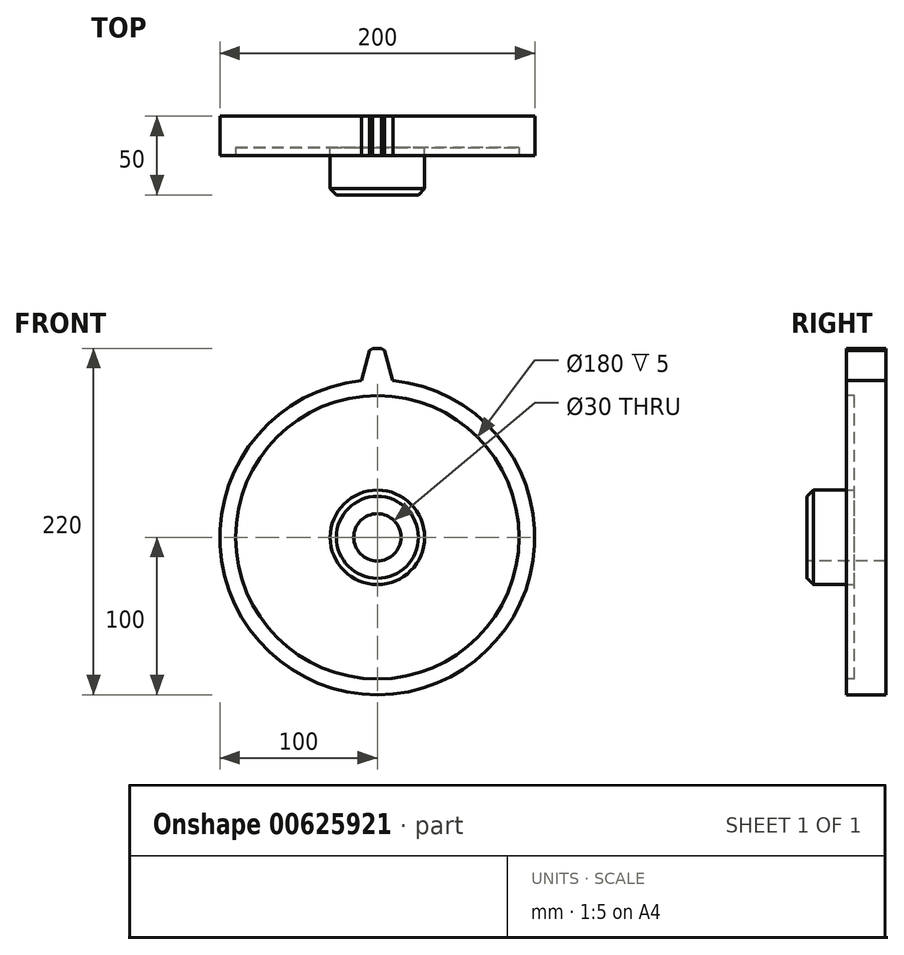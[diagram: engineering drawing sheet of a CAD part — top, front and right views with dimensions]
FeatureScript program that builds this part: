
annotation { "Feature Type Name" : "Feature", "Feature Type Description" : "" }
export const myFeature = defineFeature(function(context is Context, id is Id, definition is map)
    precondition{}
    {
        {
            var Q0;
            Q0=qCreatedBy(makeId("Front.planeOp"),FACE);
            var sketch = newSketch(context, id + "F0", { "sketchPlane" : qUnion([Q0])});
            skCircle(sketch, "E0", {"center": v(0, 0) * mm, "radius": 100 * mm});
            skSolve(sketch);
        }
        {
            var Q0;
            Q0=qCreatedBy(makeId("Front.planeOp"),FACE);
            var sketch = newSketch(context, id + "F1", { "sketchPlane" : qUnion([Q0])});
            skLineSegment(sketch, "E1", {"start": v(9.81, 99.52) * mm, "end": v(-10.17, 99.48) * mm});
            skLineSegment(sketch, "E2", {"start": v(-10.17, 99.48) * mm, "end": v(-4.72, 120) * mm});
            skLineSegment(sketch, "E3", {"start": v(-4.72, 120) * mm, "end": v(4.28, 120) * mm});
            skLineSegment(sketch, "E4", {"start": v(4.28, 120) * mm, "end": v(9.81, 99.52) * mm});
            skSolve(sketch);
        }
        {
            var Q0;
            Q0=qSketchRegion(id+"F0",true);
            extrude(context, id + "F2", {"entities" : qUnion([Q0]), "depth" : 25 * mm, "offsetDistance" : 25 * mm});
        }
        {
            var Q0;
            Q0=makeQuery(id+"F1.imprint","IMPRINT",FACE,{"disambiguationData":[TD([[makeQuery(id+"F1.imprint","IMPRINT",EDGE,{"derivedFrom":sQuery(id+"F1.wireOp",EDGE,"E1")}),-1.0]])]});
            var Q1;
            Q1=makeQuery(id+"F2.opExtrude","CAP_FACE",FACE,{"disambiguationData":[OSD([sQuery(id+"F0.wireOp",EDGE,"E0")])],"isStart":false});
            extrude(context, id + "F3", {"entities" : qUnion([Q0]), "operationType" : NewBodyOperationType.ADD, "endBound" : BoundingType.UP_TO_SURFACE, "depth" : 25 * mm, "endBoundEntityFace" : qUnion([Q1]), "offsetDistance" : 25 * mm});
        }
        {
            var Q0;
            Q0=makeQuery(id+"F3.opExtrude","SWEPT_EDGE",EDGE,{"disambiguationData":[OSD([sQuery(id+"F1.wireOp",EDGE,"E1"),sQuery(id+"F1.wireOp",EDGE,"E2")])]});
            var Q1;
            Q1=makeQuery(id+"F3.opExtrude","SWEPT_EDGE",EDGE,{"disambiguationData":[OSD([sQuery(id+"F1.wireOp",EDGE,"E1"),sQuery(id+"F1.wireOp",EDGE,"E4")])]});
            fillet(context, id + "F4", {"entities" : qUnion([Q0, Q1]), "radius" : 5 * mm, "tangentPropagation" : true, "allowEdgeOverflow" : false});
        }
        {
            var Q0;
            Q0=makeQuery(id+"F3.opExtrude","SWEPT_EDGE",EDGE,{"disambiguationData":[OSD([sQuery(id+"F1.wireOp",EDGE,"E2"),sQuery(id+"F1.wireOp",EDGE,"E3")])]});
            var Q1;
            Q1=makeQuery(id+"F3.opExtrude","SWEPT_EDGE",EDGE,{"disambiguationData":[OSD([sQuery(id+"F1.wireOp",EDGE,"E3"),sQuery(id+"F1.wireOp",EDGE,"E4")])]});
            chamfer(context, id + "F5", {"entities" : qUnion([Q0, Q1]), "width" : 2 * mm, "tangentPropagation" : true});
        }
        {
            var Q0;
            {var subQ0=sQuery(id+"F0.wireOp",EDGE,"E0");Q0=makeQuery(id+"FKvSvNCsyhTZhGM_1.19.F3.boolean.opBoolean","MERGE",FACE,{"derivedFrom":[makeQuery(id+"FKvSvNCsyhTZhGM_1.18.F3.boolean.opBoolean","MERGE",FACE,{"derivedFrom":[makeQuery(id+"FKvSvNCsyhTZhGM_1.17.F3.boolean.opBoolean","MERGE",FACE,{"derivedFrom":[makeQuery(id+"FKvSvNCsyhTZhGM_1.16.F3.boolean.opBoolean","MERGE",FACE,{"derivedFrom":[makeQuery(id+"FKvSvNCsyhTZhGM_1.15.F3.boolean.opBoolean","MERGE",FACE,{"derivedFrom":[makeQuery(id+"FKvSvNCsyhTZhGM_1.14.F3.boolean.opBoolean","MERGE",FACE,{"derivedFrom":[makeQuery(id+"FKvSvNCsyhTZhGM_1.13.F3.boolean.opBoolean","MERGE",FACE,{"derivedFrom":[makeQuery(id+"FKvSvNCsyhTZhGM_1.12.F3.boolean.opBoolean","MERGE",FACE,{"derivedFrom":[makeQuery(id+"FKvSvNCsyhTZhGM_1.11.F3.boolean.opBoolean","MERGE",FACE,{"derivedFrom":[makeQuery(id+"FKvSvNCsyhTZhGM_1.10.F3.boolean.opBoolean","MERGE",FACE,{"derivedFrom":[makeQuery(id+"FKvSvNCsyhTZhGM_1.9.F3.boolean.opBoolean","MERGE",FACE,{"derivedFrom":[makeQuery(id+"FKvSvNCsyhTZhGM_1.8.F3.boolean.opBoolean","MERGE",FACE,{"derivedFrom":[makeQuery(id+"FKvSvNCsyhTZhGM_1.7.F3.boolean.opBoolean","MERGE",FACE,{"derivedFrom":[makeQuery(id+"FKvSvNCsyhTZhGM_1.6.F3.boolean.opBoolean","MERGE",FACE,{"derivedFrom":[makeQuery(id+"FKvSvNCsyhTZhGM_1.5.F3.boolean.opBoolean","MERGE",FACE,{"derivedFrom":[makeQuery(id+"FKvSvNCsyhTZhGM_1.4.F3.boolean.opBoolean","MERGE",FACE,{"derivedFrom":[makeQuery(id+"FKvSvNCsyhTZhGM_1.3.F3.boolean.opBoolean","MERGE",FACE,{"derivedFrom":[makeQuery(id+"FKvSvNCsyhTZhGM_1.2.F3.boolean.opBoolean","MERGE",FACE,{"derivedFrom":[makeQuery(id+"FKvSvNCsyhTZhGM_1.1.F3.boolean.opBoolean","MERGE",FACE,{"derivedFrom":[makeQuery(id+"F3.boolean.opBoolean","MERGE",FACE,{"derivedFrom":[makeQuery(id+"F2.opExtrude","CAP_FACE",FACE,{"disambiguationData":[OSD([subQ0])],"isStart":false}),makeQuery(id+"F3.opExtrude","CAP_FACE",FACE,{"disambiguationData":[OSD([subQ0])],"isStart":false})]}),makeQuery(id+"FKvSvNCsyhTZhGM_1.1.F3.opExtrude","CAP_FACE",FACE,{"disambiguationData":[OSD([subQ0])],"isStart":false})]}),makeQuery(id+"FKvSvNCsyhTZhGM_1.2.F3.opExtrude","CAP_FACE",FACE,{"disambiguationData":[OSD([subQ0])],"isStart":false})]}),makeQuery(id+"FKvSvNCsyhTZhGM_1.3.F3.opExtrude","CAP_FACE",FACE,{"disambiguationData":[OSD([subQ0])],"isStart":false})]}),makeQuery(id+"FKvSvNCsyhTZhGM_1.4.F3.opExtrude","CAP_FACE",FACE,{"disambiguationData":[OSD([subQ0])],"isStart":false})]}),makeQuery(id+"FKvSvNCsyhTZhGM_1.5.F3.opExtrude","CAP_FACE",FACE,{"disambiguationData":[OSD([subQ0])],"isStart":false})]}),makeQuery(id+"FKvSvNCsyhTZhGM_1.6.F3.opExtrude","CAP_FACE",FACE,{"disambiguationData":[OSD([subQ0])],"isStart":false})]}),makeQuery(id+"FKvSvNCsyhTZhGM_1.7.F3.opExtrude","CAP_FACE",FACE,{"disambiguationData":[OSD([subQ0])],"isStart":false})]}),makeQuery(id+"FKvSvNCsyhTZhGM_1.8.F3.opExtrude","CAP_FACE",FACE,{"disambiguationData":[OSD([subQ0])],"isStart":false})]}),makeQuery(id+"FKvSvNCsyhTZhGM_1.9.F3.opExtrude","CAP_FACE",FACE,{"disambiguationData":[OSD([subQ0])],"isStart":false})]}),makeQuery(id+"FKvSvNCsyhTZhGM_1.10.F3.opExtrude","CAP_FACE",FACE,{"disambiguationData":[OSD([subQ0])],"isStart":false})]}),makeQuery(id+"FKvSvNCsyhTZhGM_1.11.F3.opExtrude","CAP_FACE",FACE,{"disambiguationData":[OSD([subQ0])],"isStart":false})]}),makeQuery(id+"FKvSvNCsyhTZhGM_1.12.F3.opExtrude","CAP_FACE",FACE,{"disambiguationData":[OSD([subQ0])],"isStart":false})]}),makeQuery(id+"FKvSvNCsyhTZhGM_1.13.F3.opExtrude","CAP_FACE",FACE,{"disambiguationData":[OSD([subQ0])],"isStart":false})]}),makeQuery(id+"FKvSvNCsyhTZhGM_1.14.F3.opExtrude","CAP_FACE",FACE,{"disambiguationData":[OSD([subQ0])],"isStart":false})]}),makeQuery(id+"FKvSvNCsyhTZhGM_1.15.F3.opExtrude","CAP_FACE",FACE,{"disambiguationData":[OSD([subQ0])],"isStart":false})]}),makeQuery(id+"FKvSvNCsyhTZhGM_1.16.F3.opExtrude","CAP_FACE",FACE,{"disambiguationData":[OSD([subQ0])],"isStart":false})]}),makeQuery(id+"FKvSvNCsyhTZhGM_1.17.F3.opExtrude","CAP_FACE",FACE,{"disambiguationData":[OSD([subQ0])],"isStart":false})]}),makeQuery(id+"FKvSvNCsyhTZhGM_1.18.F3.opExtrude","CAP_FACE",FACE,{"disambiguationData":[OSD([subQ0])],"isStart":false})]}),makeQuery(id+"FKvSvNCsyhTZhGM_1.19.F3.opExtrude","CAP_FACE",FACE,{"disambiguationData":[OSD([subQ0])],"isStart":false})]});}
            var sketch = newSketch(context, id + "F6", { "sketchPlane" : qUnion([Q0])});
            skCircle(sketch, "E5", {"center": v(0, 0) * mm, "radius": 90 * mm});
            skSolve(sketch);
        }
        {
            var Q0;
            Q0=makeQuery(id+"F6.imprint","IMPRINT",FACE,{"disambiguationData":[TD([[makeQuery(id+"F6.imprint","IMPRINT",EDGE,{"derivedFrom":sQuery(id+"F6.wireOp",EDGE,"E5")}),1.0]])]});
            extrude(context, id + "F7", {"entities" : qUnion([Q0]), "operationType" : NewBodyOperationType.REMOVE, "oppositeDirection" : true, "depth" : 5 * mm, "offsetDistance" : 25 * mm});
        }
        {
            var Q0;
            Q0=makeQuery(id+"F7.boolean.opBoolean","COPY",FACE,{"derivedFrom":makeQuery(id+"F7.opExtrude","CAP_FACE",FACE,{"disambiguationData":[OSD([sQuery(id+"F6.wireOp",EDGE,"E5")])],"isStart":false})});
            var sketch = newSketch(context, id + "F8", { "sketchPlane" : qUnion([Q0])});
            skCircle(sketch, "E6", {"center": v(0, 0) * mm, "radius": 30 * mm});
            skSolve(sketch);
        }
        {
            var Q0;
            Q0=qSketchRegion(id+"F8",true);
            extrude(context, id + "F9", {"entities" : qUnion([Q0]), "operationType" : NewBodyOperationType.ADD, "depth" : 30 * mm, "offsetDistance" : 25 * mm});
        }
        {
            var Q0;
            Q0=makeQuery(id+"F9.opExtrude","CAP_FACE",FACE,{"disambiguationData":[OSD([sQuery(id+"F8.wireOp",EDGE,"E6")])],"isStart":false});
            var sketch = newSketch(context, id + "F10", { "sketchPlane" : qUnion([Q0])});
            skCircle(sketch, "E7", {"center": v(0, 0) * mm, "radius": 15 * mm});
            skSolve(sketch);
        }
        {
            var Q0;
            Q0=qSketchRegion(id+"F10",true);
            extrude(context, id + "F11", {"entities" : qUnion([Q0]), "operationType" : NewBodyOperationType.REMOVE, "endBound" : BoundingType.THROUGH_ALL, "oppositeDirection" : true, "depth" : 25 * mm, "offsetDistance" : 25 * mm});
        }
        {
            var Q0;
            Q0=makeQuery(id+"F9.opExtrude","CAP_EDGE",EDGE,{"disambiguationData":[OSD([sQuery(id+"F8.wireOp",EDGE,"E6")])],"isStart":false});
            var Q1;
            Q1=makeQuery(id+"F11.boolean.opBoolean","COPY",EDGE,{"derivedFrom":makeQuery(id+"F11.opExtrude","CAP_EDGE",EDGE,{"disambiguationData":[OSD([sQuery(id+"F10.wireOp",EDGE,"E7")])],"isStart":true})});
            chamfer(context, id + "F12", {"entities" : qUnion([Q0, Q1]), "width" : 4 * mm, "tangentPropagation" : true});
        }
    });
